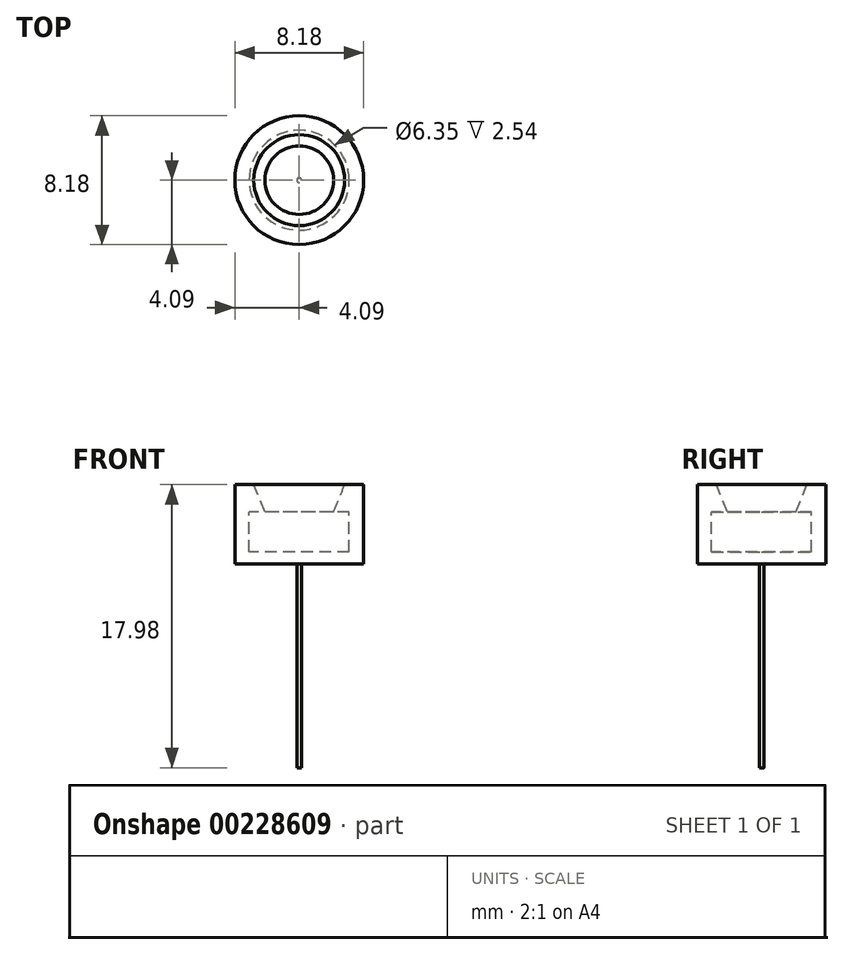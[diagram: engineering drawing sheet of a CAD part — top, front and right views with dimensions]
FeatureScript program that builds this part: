
annotation { "Feature Type Name" : "Feature", "Feature Type Description" : "" }
export const myFeature = defineFeature(function(context is Context, id is Id, definition is map)
    precondition{}
    {
        {
            var Q0;
            Q0=qCreatedBy(makeId("Front.planeOp"),FACE);
            var sketch = newSketch(context, id + "F0", { "sketchPlane" : qUnion([Q0])});
            skLineSegment(sketch, "E0", {"start": v(0, -12.95) * mm, "end": v(-0.15, -12.95) * mm});
            skLineSegment(sketch, "E1", {"start": v(-0.15, -12.95) * mm, "end": v(-0.15, 0) * mm});
            skLineSegment(sketch, "E2", {"start": v(-0.15, 0) * mm, "end": v(-4.09, 0) * mm});
            skLineSegment(sketch, "E3", {"start": v(-4.09, 0) * mm, "end": v(-4.09, 5.03) * mm});
            skLineSegment(sketch, "E4", {"start": v(-4.09, 5.03) * mm, "end": v(-2.89, 5.03) * mm});
            skLineSegment(sketch, "E5", {"start": v(-2.89, 5.03) * mm, "end": v(-2.18, 3.3) * mm});
            skLineSegment(sketch, "E6", {"start": v(-2.18, 3.3) * mm, "end": v(-3.18, 3.3) * mm});
            skLineSegment(sketch, "E7", {"start": v(-3.18, 3.3) * mm, "end": v(-3.18, 0.76) * mm});
            skLineSegment(sketch, "E8", {"start": v(-3.17, 0.76) * mm, "end": v(0, 0.76) * mm});
            skLineSegment(sketch, "E9", {"start": v(0, 0.76) * mm, "end": v(0, -12.95) * mm});
            skSolve(sketch);
        }
        {
            var Q0;
            Q0 = qSketchRegion(id + "F0", true);
            var Q1;
            Q1=sQuery(id+"F0.wireOp",EDGE,"E9");
            revolve(context, id + "F1", {"entities" : qUnion([Q0]), "axis" : qUnion([Q1]), "revolveType" : RevolveType.FULL});
        }
    });
